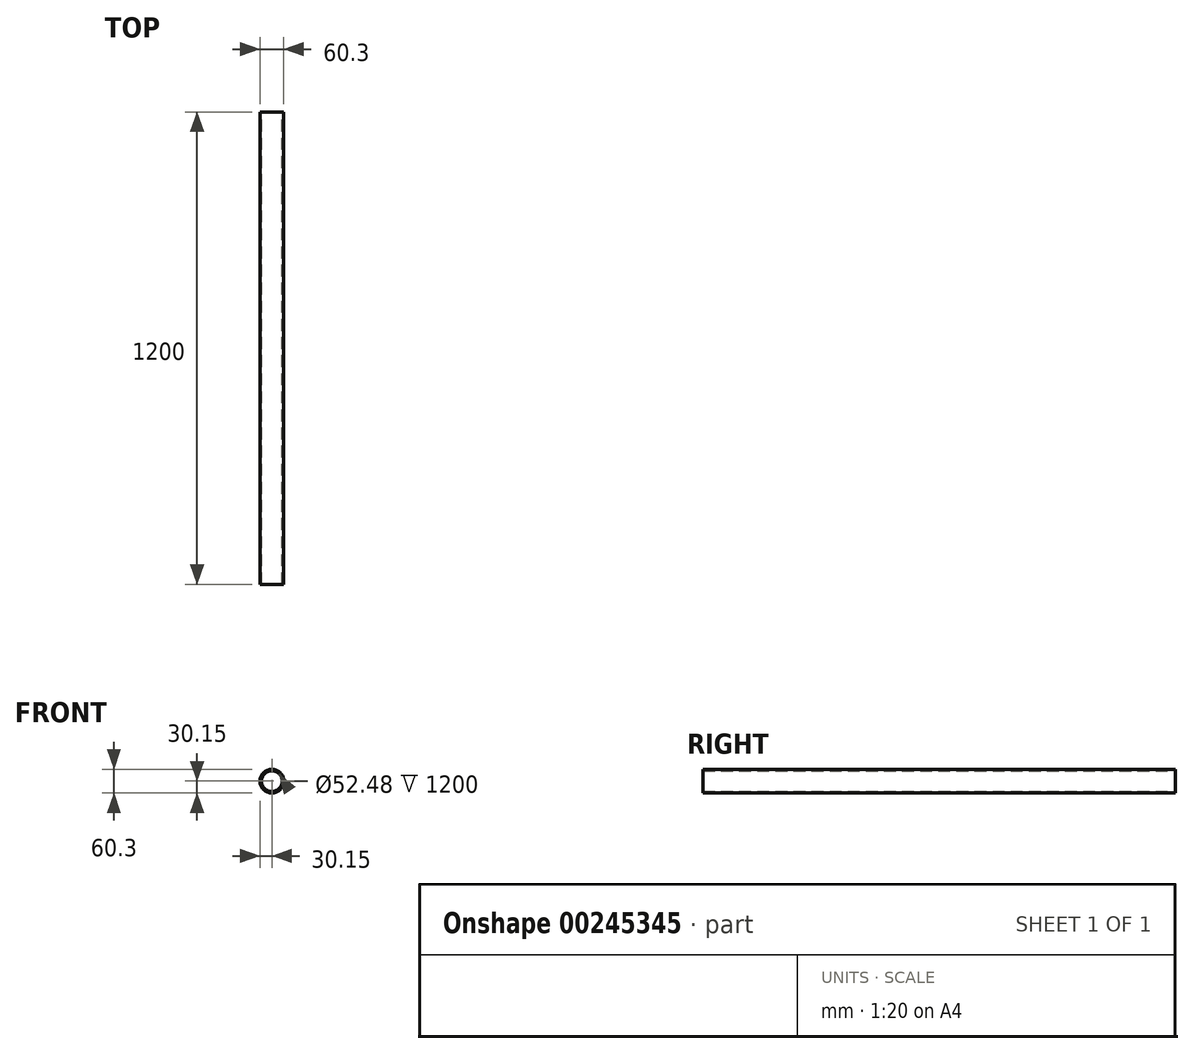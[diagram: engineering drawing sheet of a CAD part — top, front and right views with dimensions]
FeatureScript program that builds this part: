
annotation { "Feature Type Name" : "Feature", "Feature Type Description" : "" }
export const myFeature = defineFeature(function(context is Context, id is Id, definition is map)
    precondition{}
    {
        {
            var Q0;
            Q0=qCreatedBy(makeId("Front.planeOp"),FACE);
            var sketch = newSketch(context, id + "F0", { "sketchPlane" : qUnion([Q0])});
            skCircle(sketch, "E0", {"center": v(0, 0) * mm, "radius": 30.15 * mm});
            skCircle(sketch, "E1", {"center": v(0, 0) * mm, "radius": 26.24 * mm});
            skSolve(sketch);
        }
        {
            var Q0;
            Q0 = qSketchRegion(id + "F0", true);
            extrude(context, id + "F1", {"entities" : qUnion([Q0]), "depth" : 1200 * mm});
        }
    });
